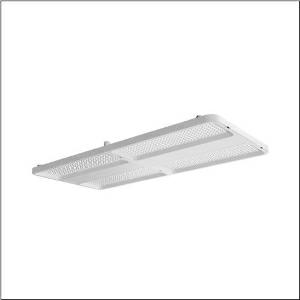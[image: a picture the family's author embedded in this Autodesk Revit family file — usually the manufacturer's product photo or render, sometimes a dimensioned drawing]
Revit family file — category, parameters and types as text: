
# Revit family: highbay_11_maxi_51hn12db4xda
name_source: partatom
category: Lighting Fixtures
units: mm (PartAtom-declared; Revit-internal decimal feet)

## family parameters
Cut with Voids When Loaded = No
Host = Face
Light Source = No
Part Type = Normal
Room Calculation Point = No
Round Connector Dimension = Use Diameter
Shared = No

## types (1)
- --- (1 x LED, 11470 lm, 57.1 W, 4000K)
    Apparent Load = 57 VA
    CIE Flux Codes = 87 98 100 100 100
    Color Rendering = 80
    Color Temperature = 4000K
    Default Elevation = 1800 mm
    Description = high bay luminaire Highbay 11 maxi; direct symmetric wide distribution, light control with lens of PMMA; UGR ≤ 25 (X = 4H | Y = 8H | S = 0.25H | reflection values 70/50/20); luminous flux: 70.000lm; light colour: 840, colour temperature: 4000K, MacAdam ≤ 2 SDCM (initial), colour rendering: CRI > 80; luminous efficacy: 187,7lm/W; rated service life: 50.000h (L95/B50) at AT= 25°C; control: DALI 2; luminaire connection: terminal, 5-pole, max. 2.5mm² (cable entry for one cable, Ø 8.5..16mm); mains connection: 230..240V, AC/DC 0/50..60Hz; connected load: 372,9W; protection rating (complete): IP66; insulation class (complete): insulation class I (protective earthing); protection symbol: D; impact resistance: IK08; certification: CE, ENEC, VDE, UKCA; luminaire for central battery installations according to DIN EN 60598-2-22, internal wiring halogen-free; luminaire LABS conformity tested according to VDMA 24364:2018-05; corresponds to IFS (International Featured Standards) requirements for safety and quality in the food industry; housing frame of high-performance plastic PA6, matt traffic white (RAL 9016); cover of PMMA; dimension (LxWxH): 946 x 442 x 72mm; permissible operating ambient temperature: -40..+50°C (reducing of maximum allowable ambient temperature of 5°C with ceiling mounting); packaging unit: 1 piece; (delivery without accessories; please order mounting accessories separately)
    Height = 72 mm  [stored 0.23622 ft]
    Lamp = 1 x LED
    Lamp Light Flux = 11470 lm
    Lamp Power = 57.1 W
    Lamp count = 1
    Length = 946 mm
    Luminous efficacy = 201 lm/W
    Manufacturer = Siteco
    ModVariant = No
    Model = 51HN12DB4XDA
    Mounting Place = Ceiling
    Mounting Type = Pendant
    Number of Poles = 1
    OnlyDefault = Yes
    Power Factor = 1
    Product Name = Highbay 11 maxi
    Product group = high bay luminaire
    ProductGroupID = 901
    Protection Class = Protection class I
    Protection Degree = IP 66
    RLX_Detail_Level = 1
    RLX_Emergency_Light_Flux = 0 lm
    RLX_Emergency_Type = 0
    RLX_Emergency_Type_DB = No
    RlxData = <blob elided: 127717 chars, md5=bb2b2816>
    Socket = socket
    Standby Power = 0 W
    System Light Flux = 11470 lm
    System Power = 57 W
    Type Comments = : DC mode (central or group accumulator) initial emergency light level
    Type Image = l_1363244.jpg
    URL = http://relux.com
    VarID = @adj_023445
    Voltage = 0 V
    Weight = 0.00 kg
    Width = 442 mm

note: [stored X ft] marks values corroborated as IEEE doubles in the binary element streams (Revit-internal decimal feet)

## geometry (parser evidence)
native form markers: Blend x4, Sweep x10
no freeform markers — native parametric forms only
